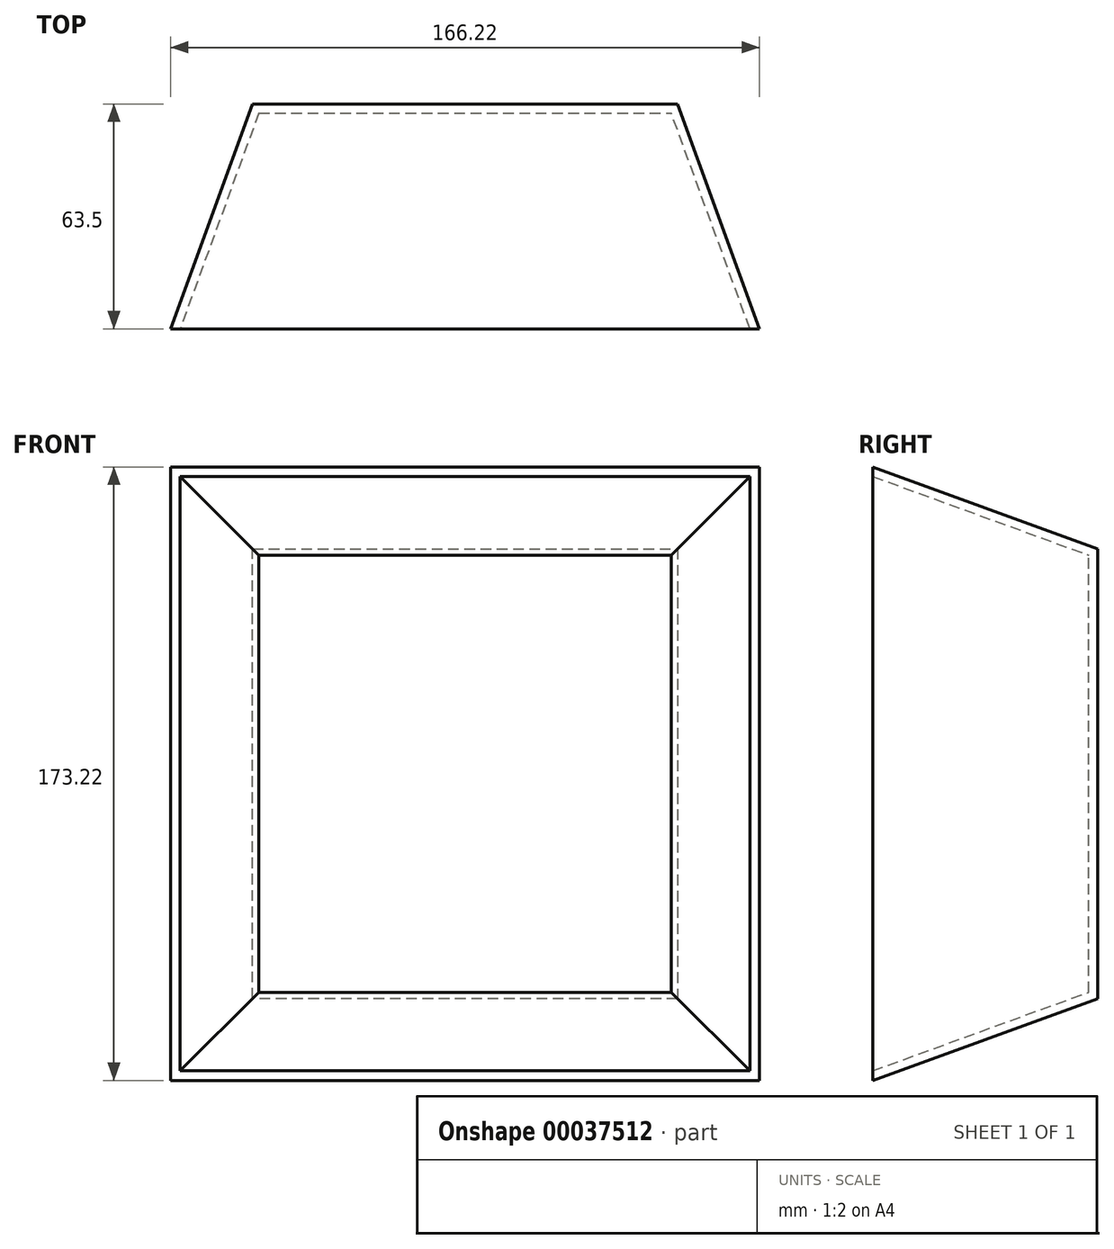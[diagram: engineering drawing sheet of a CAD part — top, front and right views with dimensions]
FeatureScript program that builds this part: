
annotation { "Feature Type Name" : "Feature", "Feature Type Description" : "" }
export const myFeature = defineFeature(function(context is Context, id is Id, definition is map)
    precondition{}
    {
        {
            var Q0;
            Q0=qCreatedBy(makeId("Front.planeOp"),FACE);
            var sketch = newSketch(context, id + "F0", { "sketchPlane" : qUnion([Q0])});
            skLineSegment(sketch, "E0.rect.bottom", {"start": v(-60, 63.5) * mm, "end": v(60, 63.5) * mm});
            skLineSegment(sketch, "E0.rect.top", {"start": v(-60, -63.5) * mm, "end": v(60, -63.5) * mm});
            skLineSegment(sketch, "E0.rect.left", {"start": v(-60, 63.5) * mm, "end": v(-60, -63.5) * mm});
            skLineSegment(sketch, "E0.rect.right", {"start": v(60, 63.5) * mm, "end": v(60, -63.5) * mm});
            skPoint(sketch, "E0.rect.middle", {"position": v(0, 0) * mm});
            skSolve(sketch);
        }
        {
            var Q0;
            Q0=makeQuery(id+"F0.imprint","IMPRINT",FACE,{"disambiguationData":[TD([[makeQuery(id+"F0.imprint","IMPRINT",EDGE,{"derivedFrom":sQuery(id+"F0.wireOp",EDGE,"E0.rect.bottom")}),-1.0]])]});
            extrude(context, id + "F1", {"entities" : qUnion([Q0]), "depth" : 63.5 * mm, "hasDraft" : true, "draftAngle" : 20 * degree});
        }
        {
            var Q0;
            Q0=makeQuery(id+"F1.opExtrude","CAP_FACE",FACE,{"disambiguationData":[OSD([sQuery(id+"F0.wireOp",EDGE,"E0.rect.bottom"),sQuery(id+"F0.wireOp",EDGE,"E0.rect.top"),sQuery(id+"F0.wireOp",EDGE,"E0.rect.left"),sQuery(id+"F0.wireOp",EDGE,"E0.rect.right")])],"isStart":false});
            shell(context, id + "F2", {"entities" : qUnion([Q0]), "thickness" : 2.54 * mm});
        }
    });
